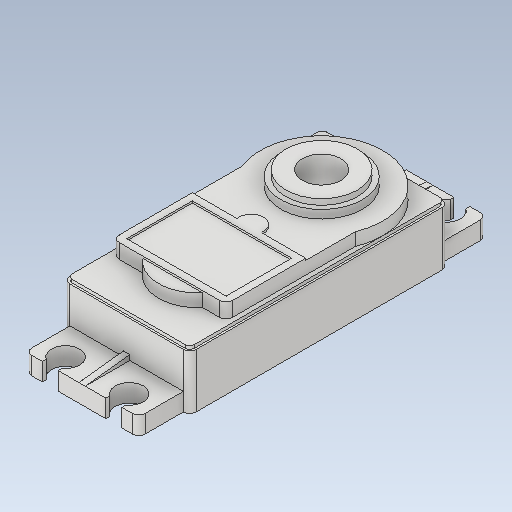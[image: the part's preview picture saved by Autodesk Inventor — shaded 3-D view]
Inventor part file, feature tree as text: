
AUTODESK INVENTOR PART (.ipt)
format: ipt  version: 2020 (Build 240168000, 168)  size: 310,272 bytes
history: native  units: mm
features: sketch x13, extrude x12, mirror x2, fillet x2, other x1
ambient origin geometry x8: Origin, YZ Plane, XZ Plane, XY Plane, X Axis, Y Axis, Z Axis, Center Point
bodies: Body1 (feature_tree)
feature tree (30):
  other  "Sólido1"
  extrude  "Extrusión1"  Depth=40.6mm
  extrude  "Extrusión2"  Depth=9.0mm
  extrude  "Extrusión5"  Depth=9.0mm TaperAngle=0.0deg
  extrude  "Extrusión6"  Depth=2.8mm TaperAngle=0.0deg
  extrude  "Extrusión7"  Depth=2.8mm TaperAngle=0.0deg
  mirror  "Simetría3"
  mirror  "Simetría4"
  extrude  "Extrusión8"  Depth=1.0mm TaperAngle=0.0deg
  extrude  "Extrusión9"  Depth=9.6mm
  extrude  "Extrusión10"  Depth=2.0mm TaperAngle=0.0deg
  extrude  "Extrusión11"  Depth=9.4mm
  extrude  "Extrusión12"  Depth=2.0mm
  extrude  "Extrusión13"  Depth=1.3mm
  extrude  "Extrusión14"  Depth=17.8mm
  fillet  "Empalme1"  Radius=12.5mm
  fillet  "Empalme2"  Radius=1.1mm
  sketch  "Boceto18"  dims[d64=0.3mm d65=0.0mm d66=3.88mm d67=1.44mm d68=0.3mm d69=0.0mm d70=0.3mm d71=0.5mm d72=0.0mm d73=1.0mm d74=0.7mm]
  sketch  "Boceto1"  dims[d0=19.8mm d1=40.6mm]
  sketch  "Boceto2"  dims[d2=9.0mm d3=0.0mm d4=6.0mm]
  sketch  "Boceto5"  dims[d5=10.0mm d6=9.0mm d7=0.0mm]
  sketch  "Boceto6"  dims[d23=17.8mm d24=7.0mm d25=2.8mm d26=0.0mm]
  sketch  "Boceto8"  dims[d27=4.4mm d28=2.41mm d29=5.0mm d30=2.65mm d31=0.6mm d32=2.8mm d33=0.0mm]
  sketch  "Boceto9"  dims[d34=0.8mm d35=1.0mm d36=0.0mm]
  sketch  "Boceto11"  dims[d37=19.2mm d40=9.6mm]
  sketch  "Boceto12"  dims[d42=20.3mm d43=2.0mm d44=0.0mm]
  sketch  "Boceto13"  dims[d50=2.2mm d51=9.4mm]
  sketch  "Boceto15"  dims[d52=2.0mm d53=0.0mm d54=12.8mm]
  sketch  "Boceto16"  dims[d55=1.3mm d56=0.0mm d57=11.2mm]
  sketch  "Boceto17"  dims[d58=0.9mm d59=0.0mm d61=17.8mm d62=12.5mm d63=1.1mm]
